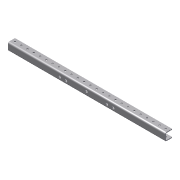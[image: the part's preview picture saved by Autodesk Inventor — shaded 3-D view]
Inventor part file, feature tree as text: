
AUTODESK INVENTOR PART (.ipt)
format: ipt  version: 2013 (Build 170138000, 138)  size: 213,504 bytes
history: native  units: in
note: dims shown in document units (in); Inventor stores cm internally (conversion verified against a paired STEP export)
features: projected_geometry x8, extrude x2, sketch x2, other x1, imported_body x1
ambient origin geometry x8: Origin, YZ Plane, XZ Plane, XY Plane, X Axis, Y Axis, Z Axis, Center Point
feature tree (14):
  other  "Short C Channel for drive1"
  extrude  "Extrusion1"  TaperAngle=0.0deg  [1 undecoded]
  extrude  "Extrusion2"  [1 undecoded]
  imported_body  "Base1"
  sketch  "Sketch1"  dims[d1=0.0in d3=0.0in]
  projected_geometry  "Projected Loop1"
  projected_geometry  "Projected Loop2"
  projected_geometry  "Projected Loop3"
  projected_geometry  "Projected Loop4"
  sketch  "Sketch2"
  projected_geometry  "Projected Loop5"
  projected_geometry  "Projected Loop6"
  projected_geometry  "Projected Loop7"
  projected_geometry  "Projected Loop8"
note: 2 required parameter values undecoded (feature->parameter linkage not recoverable at this tier; creation-order binding heuristic only, values carry confidence <= 0.55)
